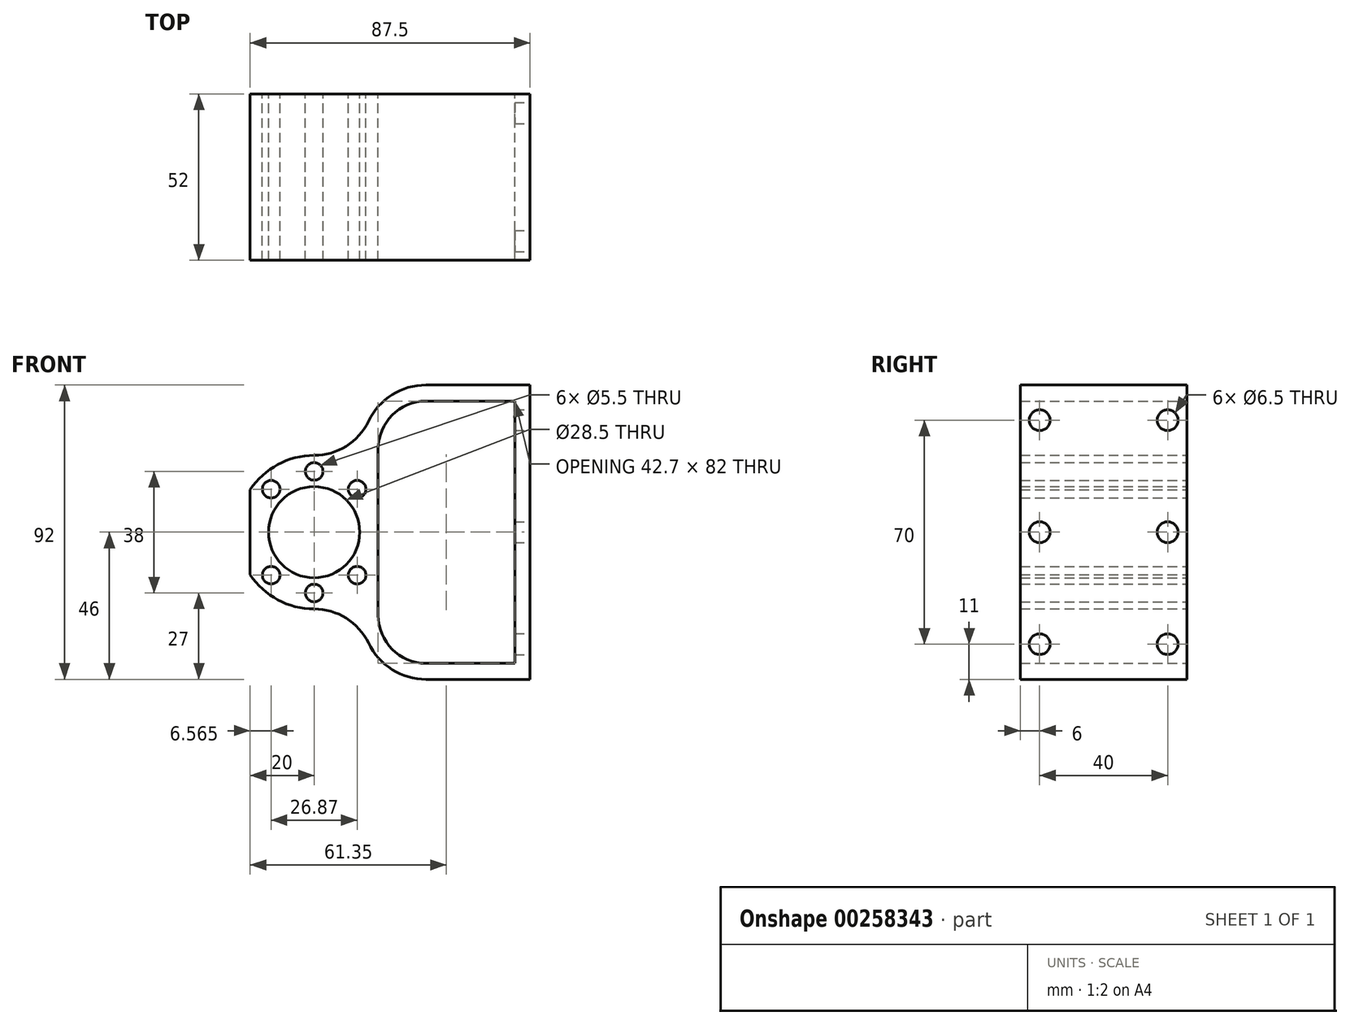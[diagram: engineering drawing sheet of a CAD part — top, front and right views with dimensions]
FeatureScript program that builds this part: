
annotation { "Feature Type Name" : "Feature", "Feature Type Description" : "" }
export const myFeature = defineFeature(function(context is Context, id is Id, definition is map)
    precondition{}
    {
        {
            var Q0;
            Q0=qCreatedBy(makeId("Front.planeOp"),FACE);
            var sketch = newSketch(context, id + "F0", { "sketchPlane" : qUnion([Q0])});
            skCircle(sketch, "E0", {"center": v(0, 0) * mm, "radius": 14.25 * mm, "construction": true});
            skCircle(sketch, "E1", {"center": v(0, 0) * mm, "radius": 19 * mm, "construction": true});
            skLineSegment(sketch, "E2", {"start": v(0, 19) * mm, "end": v(0, -19) * mm, "construction": true});
            skLineSegment(sketch, "E3", {"start": v(19, 0) * mm, "end": v(-19, 0) * mm, "construction": true});
            skLineSegment(sketch, "E4", {"start": v(-13.44, 13.44) * mm, "end": v(13.44, -13.44) * mm, "construction": true});
            skCircle(sketch, "E5", {"center": v(0, 19) * mm, "radius": 2.75 * mm, "construction": true});
            skCircle(sketch, "E6", {"center": v(-13.44, 13.44) * mm, "radius": 2.75 * mm, "construction": true});
            skCircle(sketch, "E7", {"center": v(13.44, 13.44) * mm, "radius": 2.75 * mm, "construction": true});
            skCircle(sketch, "E8.MirrorC", {"center": v(-13.44, -13.44) * mm, "radius": 2.75 * mm, "construction": true});
            skCircle(sketch, "E9.MirrorC", {"center": v(0, -19) * mm, "radius": 2.75 * mm, "construction": true});
            skCircle(sketch, "E10.MirrorC", {"center": v(13.44, -13.44) * mm, "radius": 2.75 * mm, "construction": true});
            skArc(sketch, "E11", {"start": v(-20, -13.27) * mm, "mid": v(0, -24) * mm, "end": v(20, -13.27) * mm, "construction": true});
            skLineSegment(sketch, "E12", {"start": v(-20, 13.27) * mm, "end": v(-20, -13.27) * mm, "construction": true});
            skLineSegment(sketch, "E13", {"start": v(20, 13.27) * mm, "end": v(20, -13.27) * mm, "construction": true});
            skArc(sketch, "E14.trimOffspring", {"start": v(20, 13.27) * mm, "mid": v(0, 24) * mm, "end": v(-20, 13.27) * mm, "construction": true});
            skLineSegment(sketch, "E15", {"start": v(30, 35) * mm, "end": v(30, -35) * mm, "construction": true});
            skPoint(sketch, "E16", {"position": v(30, 0) * mm});
            skLineSegment(sketch, "E17", {"start": v(30, 35) * mm, "end": v(35, 35) * mm, "construction": true});
            skLineSegment(sketch, "E18", {"start": v(35, 35) * mm, "end": v(35, -35) * mm, "construction": true});
            skLineSegment(sketch, "E19", {"start": v(35, -35) * mm, "end": v(30, -35) * mm, "construction": true});
            skLineSegment(sketch, "E20.bottom", {"start": v(35, -40) * mm, "end": v(62.5, -40) * mm, "construction": true});
            skLineSegment(sketch, "E20.top", {"start": v(35, 40) * mm, "end": v(62.5, 40) * mm, "construction": true});
            skLineSegment(sketch, "E20.left", {"start": v(35, -40) * mm, "end": v(35, 40) * mm, "construction": true});
            skLineSegment(sketch, "E20.right", {"start": v(62.5, -40) * mm, "end": v(62.5, 40) * mm, "construction": true});
            skPoint(sketch, "E21", {"position": v(35, 0) * mm});
            skSolve(sketch);
        }
        {
            var Q0;
            Q0=qCreatedBy(makeId("Front.planeOp"),FACE);
            var sketch = newSketch(context, id + "F1", { "sketchPlane" : qUnion([Q0])});
            skLineSegment(sketch, "E22.0", {"start": v(-20, 13.27) * mm, "end": v(-20, -13.27) * mm, "construction": true});
            skLineSegment(sketch, "E23.left", {"start": v(-20, 13.27) * mm, "end": v(-20, -13.27) * mm});
            skLineSegment(sketch, "E23.right", {"start": v(67.5, 46) * mm, "end": v(67.5, -46) * mm});
            skLineSegment(sketch, "E24", {"start": v(-20, 0) * mm, "end": v(67.5, 0) * mm, "construction": true});
            skLineSegment(sketch, "E25.0", {"start": v(20, 13.27) * mm, "end": v(20, -13.27) * mm, "construction": true});
            skCircle(sketch, "E26.0", {"center": v(0, 0) * mm, "radius": 14.25 * mm});
            skCircle(sketch, "E26.1", {"center": v(13.44, 13.44) * mm, "radius": 2.75 * mm});
            skCircle(sketch, "E26.2", {"center": v(0, 19) * mm, "radius": 2.75 * mm});
            skCircle(sketch, "E26.3", {"center": v(-13.44, 13.44) * mm, "radius": 2.75 * mm});
            skCircle(sketch, "E26.4", {"center": v(-13.44, -13.44) * mm, "radius": 2.75 * mm});
            skCircle(sketch, "E26.5", {"center": v(0, -19) * mm, "radius": 2.75 * mm});
            skCircle(sketch, "E26.6", {"center": v(13.44, -13.44) * mm, "radius": 2.75 * mm});
            skArc(sketch, "E27.0", {"start": v(0, 24) * mm, "mid": v(-11.35, 21.15) * mm, "end": v(-20, 13.27) * mm});
            skPoint(sketch, "E28.newPointA", {"position": v(20, 13.27) * mm});
            skArc(sketch, "E28.filletArc", {"start": v(0, 24) * mm, "mid": v(10.03, 26.89) * mm, "end": v(16.98, 34.67) * mm});
            skLineSegment(sketch, "E29", {"start": v(35, 46) * mm, "end": v(67.5, 46) * mm});
            skArc(sketch, "E30.filletArc", {"start": v(35, 46) * mm, "mid": v(24.36, 42.93) * mm, "end": v(16.98, 34.67) * mm});
            skLineSegment(sketch, "E31.bottom", {"start": v(62.7, 41) * mm, "end": v(35, 41) * mm});
            skLineSegment(sketch, "E31.left", {"start": v(62.7, 41) * mm, "end": v(62.7, -41) * mm});
            skLineSegment(sketch, "E31.right", {"start": v(20, 26) * mm, "end": v(20, -26) * mm});
            skPoint(sketch, "E32.visualSharp", {"position": v(20, 41) * mm});
            skArc(sketch, "E32.filletArc", {"start": v(35, 41) * mm, "mid": v(24.4, 36.6) * mm, "end": v(20, 26) * mm});
            skArc(sketch, "E33.MirrorCS", {"start": v(0, -24) * mm, "mid": v(-11.35, -21.15) * mm, "end": v(-20, -13.27) * mm});
            skArc(sketch, "E34.MirrorCS", {"start": v(0, -24) * mm, "mid": v(10.03, -26.89) * mm, "end": v(16.98, -34.67) * mm});
            skArc(sketch, "E35.MirrorCS", {"start": v(35, -46) * mm, "mid": v(24.36, -42.93) * mm, "end": v(16.98, -34.67) * mm});
            skLineSegment(sketch, "E36.MirrorCS", {"start": v(35, -46) * mm, "end": v(67.5, -46) * mm});
            skArc(sketch, "E37.MirrorCS", {"start": v(35, -41) * mm, "mid": v(24.4, -36.6) * mm, "end": v(20, -26) * mm});
            skLineSegment(sketch, "E38.MirrorCS", {"start": v(62.7, -41) * mm, "end": v(35, -41) * mm});
            skLineSegment(sketch, "E39.0", {"start": v(62.5, -40) * mm, "end": v(62.5, 40) * mm, "construction": true});
            skSolve(sketch);
        }
        {
            var Q0;
            Q0=qSketchRegion(id+"F1",true);
            extrude(context, id + "F2", {"entities" : qUnion([Q0]), "depth" : 52 * mm});
        }
        {
            var Q0;
            Q0=makeQuery(id+"F2.opExtrude","SWEPT_FACE",FACE,{"disambiguationData":[OSD([sQuery(id+"F1.wireOp",EDGE,"E23.right")])]});
            var sketch = newSketch(context, id + "F3", { "sketchPlane" : qUnion([Q0])});
            skLineSegment(sketch, "E40", {"start": v(-26, 46) * mm, "end": v(-26, -46) * mm, "construction": true});
            skLineSegment(sketch, "E41", {"start": v(0, 0) * mm, "end": v(-52, 0) * mm, "construction": true});
            skCircle(sketch, "E42", {"center": v(-46, 35) * mm, "radius": 3.25 * mm});
            skCircle(sketch, "E43", {"center": v(-46, 0) * mm, "radius": 3.25 * mm});
            skCircle(sketch, "E44.MirrorC", {"center": v(-46, -35) * mm, "radius": 3.25 * mm});
            skCircle(sketch, "E45.MirrorC", {"center": v(-6, 35) * mm, "radius": 3.25 * mm});
            skCircle(sketch, "E46.MirrorC", {"center": v(-6, 0) * mm, "radius": 3.25 * mm});
            skCircle(sketch, "E47.MirrorC", {"center": v(-6, -35) * mm, "radius": 3.25 * mm});
            skSolve(sketch);
        }
        {
            var Q0;
            Q0=qSketchRegion(id+"F3",true);
            extrude(context, id + "F4", {"entities" : qUnion([Q0]), "operationType" : NewBodyOperationType.REMOVE, "endBound" : BoundingType.UP_TO_NEXT, "oppositeDirection" : true, "depth" : 25 * mm});
        }
    });
